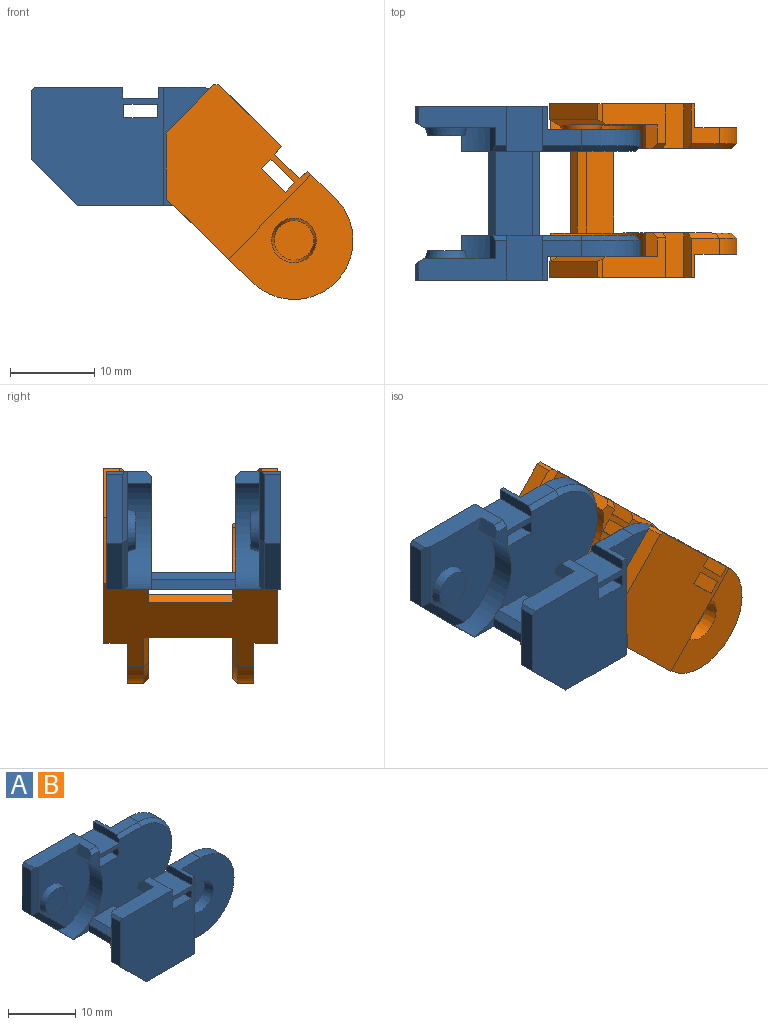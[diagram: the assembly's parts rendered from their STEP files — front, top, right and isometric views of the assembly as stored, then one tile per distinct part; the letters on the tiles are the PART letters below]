
ASSEMBLY  parts=2 mates=1
PART A: 70 faces, bbox 26.7x20.6x14 mm
  f0: plane 15.7x14mm, normal (0,-1,0), area 192.7mm2, adj f1,f4,f15,f17,f23,f24,f28,f32
  f1: plane 20.6x14.2mm, normal (0,0,-1), area 182.1mm2, adj f0,f2,f7,f10,f11,f16,f17,f24
  f2: plane 3.44x1.4mm, normal (0,1,0), area 1.6mm2, adj f1,f3,f10,f14,f24
  f3: cylinder r=7mm len=12.56mm, axis (0,1,0), area 47.2mm2, adj f2,f5,f8,f20,f24,f25,f26
  f4: plane 4.7x4.6mm, normal (0,0,1), area 10.4mm2, adj f0,f6,f7,f16,f17,f34
  f5: plane 17.2x12.8mm, normal (0,1,0), area 163.6mm2, adj f3,f6,f11,f12,f13,f25,f29,f30
  f6: plane 4.6x0.6mm, normal (0,0.71,0.71), area 3.9mm2, adj f4,f5,f30,f34
  f7: plane 14x11mm, normal (0,-1,0), area 110.9mm2, adj f1,f4,f16,f17,f19
  f8: plane 0.7x0.6mm, normal (0,-1,0), area 0mm2, adj f3,f12,f14
  f9: plane 0.7x0.6mm, normal (0,1,0), area 0mm2, adj f12,f14,f41
  f10: plane 10x1.2mm, normal (-1,0,0), area 12mm2, adj f1,f2,f14,f40
  f11: plane 11.2x1.2mm, normal (1,0,0), area 12.4mm2, adj f1,f5,f13,f31,f43,f62
  f12: plane 10x4.4mm, normal (0,0,1), area 44mm2, adj f5,f8,f9,f13,f14,f43
  f13: plane 10x0.8mm, normal (0.71,0,0.71), area 11.3mm2, adj f5,f11,f12,f43
  f14: plane 10x0.8mm, normal (-0.71,0,0.71), area 11.3mm2, adj f2,f8,f9,f10,f12,f40
  f15: plane 10.5x4.7mm, normal (0,0,1), area 29.2mm2, adj f0,f20,f25,f27,f28,f29,f33
  f16: cylinder r=7mm len=14mm, axis (0,1,0), area 41.8mm2, adj f1,f4,f7,f30
  f17: plane 14x2.8mm, normal (1,0,0), area 39.2mm2, adj f0,f1,f4,f7
  f18: plane 4.7x4.7mm, normal (0,-1,0), area 17.3mm2, adj f19
  f19: cone r=2.35mm half-angle=10.6deg, axis (0,-1,0), area 25.6mm2, adj f7,f18
  f20: plane 13.73x10.7mm, normal (0,1,0), area 94.2mm2, adj f3,f15,f22,f25,f26,f27
  f21: plane 4.4x4.4mm, normal (0,1,0), area 15.2mm2, adj f22
  f22: cone r=2.5mm half-angle=16.7deg, axis (0,-1,0), area 15.4mm2, adj f20,f21
  f23: plane 8.1x1.9mm, normal (-1,0,0), area 15.4mm2, adj f0,f24,f27,f28
  f24: plane 5.5x5.5mm, normal (-0.71,0,-0.71), area 15mm2, adj f0,f1,f2,f3,f23,f26
  f25: plane 2.8x1.4mm, normal (-0.92,0,0.39), area 4.1mm2, adj f3,f5,f15,f20,f29
  f26: plane 6.66x5.89mm, normal (-0.36,0.86,-0.36), area 9.2mm2, adj f3,f20,f24,f27
  f27: plane 8.5x1mm, normal (-0.51,0.86,0), area 9.6mm2, adj f15,f20,f23,f26,f28
  f28: plane 2.14x0.4mm, normal (-0.71,0,0.71), area 1.1mm2, adj f0,f15,f23,f27
  f29: plane 1.66x0.6mm, normal (0,0.71,0.71), area 1.3mm2, adj f5,f15,f25,f33
  f30: cone r=7mm half-angle=45deg, axis (0,-1,0), area 17.9mm2, adj f5,f6,f16,f31
  f31: plane 5x0.6mm, normal (0,0.71,-0.71), area 4.2mm2, adj f1,f5,f11,f30
  f32: plane 5.3x4.2mm, normal (0,0,1), area 22.3mm2, adj f0,f5,f33,f34
  f33: plane 5.3x1.3mm, normal (1,0,0), area 6.7mm2, adj f0,f5,f15,f29,f32
  f34: plane 5.3x1.3mm, normal (-1,0,0), area 6.7mm2, adj f0,f4,f5,f6,f32
  f35: plane 5.3x1.6mm, normal (-1,0,0), area 8.5mm2, adj f0,f5,f36,f38
  f36: plane 5.3x4mm, normal (0,0,-1), area 21.2mm2, adj f0,f5,f35,f37
  f37: plane 5.3x1.6mm, normal (1,0,0), area 8.5mm2, adj f0,f5,f36,f38
  f38: plane 5.3x4mm, normal (0,0,1), area 21.2mm2, adj f0,f5,f35,f37
  f39: plane 15.7x14mm, normal (0,1,0), area 192.7mm2, adj f1,f42,f46,f48,f54,f55,f59,f63
  f40: plane 3.44x1.4mm, normal (0,-1,0), area 1.6mm2, adj f1,f10,f14,f41,f55
  f41: cylinder r=7mm len=12.56mm, axis (0,-1,0), area 47.2mm2, adj f9,f40,f43,f51,f55,f56,f57
  f42: plane 4.7x4.6mm, normal (0,0,1), area 10.4mm2, adj f39,f44,f45,f47,f48,f65
  f43: plane 17.2x12.8mm, normal (0,-1,0), area 163.6mm2, adj f11,f12,f13,f41,f44,f56,f60,f61
  f44: plane 4.6x0.6mm, normal (0,-0.71,0.71), area 3.9mm2, adj f42,f43,f61,f65
  f45: plane 14x11mm, normal (0,1,0), area 110.9mm2, adj f1,f42,f47,f48,f50
  f46: plane 10.5x4.7mm, normal (0,0,1), area 29.2mm2, adj f39,f51,f56,f58,f59,f60,f64
  f47: cylinder r=7mm len=14mm, axis (0,-1,0), area 41.8mm2, adj f1,f42,f45,f61
  f48: plane 14x2.8mm, normal (1,0,0), area 39.2mm2, adj f1,f39,f42,f45
  f49: plane 4.7x4.7mm, normal (0,1,0), area 17.3mm2, adj f50
  f50: cone r=2.35mm half-angle=10.6deg, axis (0,1,0), area 25.6mm2, adj f45,f49
  f51: plane 13.73x10.7mm, normal (0,-1,0), area 94.2mm2, adj f41,f46,f53,f56,f57,f58
  f52: plane 4.4x4.4mm, normal (0,-1,0), area 15.2mm2, adj f53
  f53: cone r=2.5mm half-angle=16.7deg, axis (0,1,0), area 15.4mm2, adj f51,f52
  f54: plane 8.1x1.9mm, normal (-1,0,0), area 15.4mm2, adj f39,f55,f58,f59
  f55: plane 5.5x5.5mm, normal (-0.71,0,-0.71), area 15mm2, adj f1,f39,f40,f41,f54,f57
  f56: plane 2.8x1.4mm, normal (-0.92,0,0.39), area 4.1mm2, adj f41,f43,f46,f51,f60
  f57: plane 6.66x5.89mm, normal (-0.36,-0.86,-0.36), area 9.2mm2, adj f41,f51,f55,f58
  f58: plane 8.5x1mm, normal (-0.51,-0.86,0), area 9.6mm2, adj f46,f51,f54,f57,f59
  f59: plane 2.14x0.4mm, normal (-0.71,0,0.71), area 1.1mm2, adj f39,f46,f54,f58
  f60: plane 1.66x0.6mm, normal (0,-0.71,0.71), area 1.3mm2, adj f43,f46,f56,f64
  f61: cone r=7mm half-angle=45deg, axis (0,1,0), area 17.9mm2, adj f43,f44,f47,f62
  f62: plane 5x0.6mm, normal (0,-0.71,-0.71), area 4.2mm2, adj f1,f11,f43,f61
  f63: plane 5.3x4.2mm, normal (0,0,1), area 22.3mm2, adj f39,f43,f64,f65
  f64: plane 5.3x1.3mm, normal (1,0,0), area 6.7mm2, adj f39,f43,f46,f60,f63
  f65: plane 5.3x1.3mm, normal (-1,0,0), area 6.7mm2, adj f39,f42,f43,f44,f63
  f66: plane 5.3x1.6mm, normal (-1,0,0), area 8.5mm2, adj f39,f43,f67,f69
  f67: plane 5.3x4mm, normal (0,0,-1), area 21.2mm2, adj f39,f43,f66,f68
  f68: plane 5.3x1.6mm, normal (1,0,0), area 8.5mm2, adj f39,f43,f67,f69
  f69: plane 5.3x4mm, normal (0,0,1), area 21.2mm2, adj f39,f43,f66,f68
PART B: same geometry as A
PLACE A t=(-1.61,10.54,-4.64)mm fixed
PLACE B rot(axis=(0,1,0),44.2deg) t=(7.25,10.84,-8.23)mm
MATE revolute A.f16 <-> B.f22  axis (0,-1,0) through (6.39,3.04,2.36)mm
